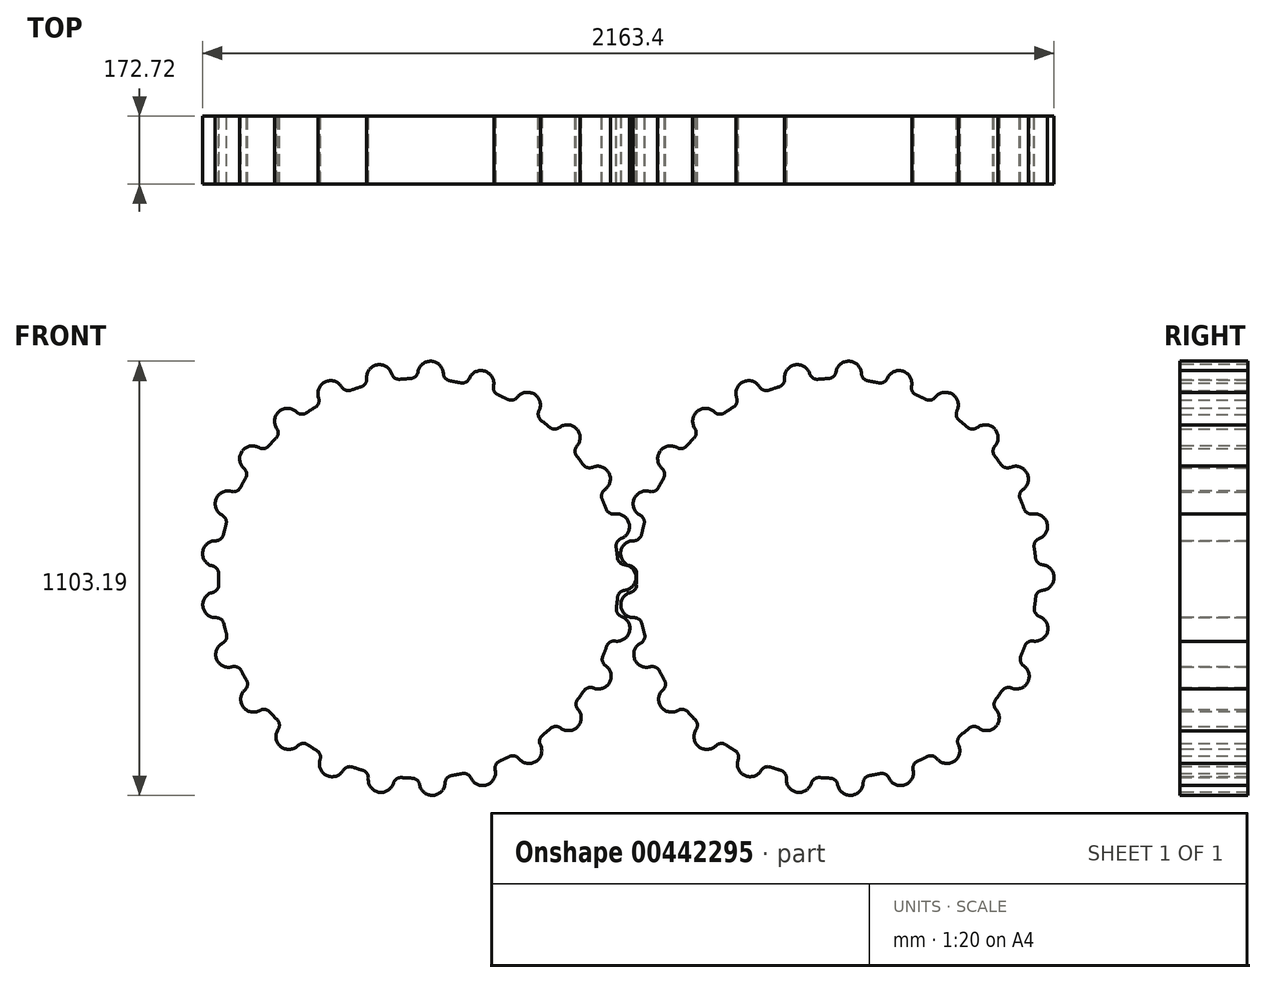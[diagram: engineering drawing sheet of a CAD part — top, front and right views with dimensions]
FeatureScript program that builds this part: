
annotation { "Feature Type Name" : "Feature", "Feature Type Description" : "" }
export const myFeature = defineFeature(function(context is Context, id is Id, definition is map)
    precondition{}
    {
        {
            var Q0;
            Q0=qCreatedBy(makeId("Front.planeOp"),FACE);
            var sketch = newSketch(context, id + "F0", { "sketchPlane" : qUnion([Q0])});
            skArc(sketch, "E0", {"start": v(0, 508) * mm, "mid": v(-33.99, 506.86) * mm, "end": v(-67.82, 503.45) * mm});
            skArc(sketch, "E1", {"start": v(59.51, 504.5) * mm, "mid": v(32.42, 551.67) * mm, "end": v(0, 508) * mm});
            skArc(sketch, "E2.1.0", {"start": v(-67.82, 503.45) * mm, "mid": v(-105.79, 542.4) * mm, "end": v(-126.33, 492.04) * mm});
            skArc(sketch, "E2.2.0", {"start": v(-190.9, 470.77) * mm, "mid": v(-237.35, 499.05) * mm, "end": v(-244.73, 445.16) * mm});
            skArc(sketch, "E2.3.0", {"start": v(-301.97, 408.5) * mm, "mid": v(-354, 424.35) * mm, "end": v(-347.75, 370.32) * mm});
            skArc(sketch, "E2.4.0", {"start": v(-394.08, 320.57) * mm, "mid": v(-448.42, 322.98) * mm, "end": v(-428.92, 272.2) * mm});
            skArc(sketch, "E2.5.0", {"start": v(-461.42, 212.5) * mm, "mid": v(-514.65, 201.31) * mm, "end": v(-483.14, 156.98) * mm});
            skArc(sketch, "E2.6.0", {"start": v(-499.77, 91.07) * mm, "mid": v(-548.54, 67) * mm, "end": v(-507, 31.9) * mm});
            skArc(sketch, "E2.7.0", {"start": v(-506.72, -36.08) * mm, "mid": v(-547.97, -71.52) * mm, "end": v(-499, -95.19) * mm});
            skArc(sketch, "E2.8.0", {"start": v(-481.83, -160.96) * mm, "mid": v(-512.97, -205.55) * mm, "end": v(-459.65, -216.3) * mm});
            skArc(sketch, "E2.9.0", {"start": v(-426.66, -275.73) * mm, "mid": v(-445.74, -326.66) * mm, "end": v(-391.42, -323.81) * mm});
            skArc(sketch, "E2.10.0", {"start": v(-344.68, -373.17) * mm, "mid": v(-350.5, -427.25) * mm, "end": v(-298.6, -410.98) * mm});
            skArc(sketch, "E2.11.0", {"start": v(-241.05, -447.17) * mm, "mid": v(-233.23, -501) * mm, "end": v(-187, -472.33) * mm});
            skArc(sketch, "E2.12.0", {"start": v(-122.27, -493.07) * mm, "mid": v(-101.31, -543.26) * mm, "end": v(-63.67, -504) * mm});
            skArc(sketch, "E2.13.0", {"start": v(4.19, -507.98) * mm, "mid": v(36.97, -551.38) * mm, "end": v(63.67, -504) * mm});
            skArc(sketch, "E2.14.0", {"start": v(130.39, -490.98) * mm, "mid": v(172.94, -524.87) * mm, "end": v(187, -472.33) * mm});
            skArc(sketch, "E2.15.0", {"start": v(248.4, -443.13) * mm, "mid": v(298.03, -465.37) * mm, "end": v(298.6, -410.98) * mm});
            skArc(sketch, "E2.16.0", {"start": v(350.8, -367.44) * mm, "mid": v(404.4, -376.63) * mm, "end": v(391.42, -323.81) * mm});
            skArc(sketch, "E2.17.0", {"start": v(431.15, -268.65) * mm, "mid": v(485.36, -264.23) * mm, "end": v(459.65, -216.3) * mm});
            skArc(sketch, "E2.18.0", {"start": v(484.42, -153) * mm, "mid": v(535.82, -135.22) * mm, "end": v(499, -95.19) * mm});
            skArc(sketch, "E2.19.0", {"start": v(507.24, -27.71) * mm, "mid": v(552.62, 2.28) * mm, "end": v(507, 31.9) * mm});
            skArc(sketch, "E2.20.0", {"start": v(498.2, 99.3) * mm, "mid": v(534.69, 139.64) * mm, "end": v(483.14, 156.98) * mm});
            skArc(sketch, "E2.21.0", {"start": v(457.85, 220.08) * mm, "mid": v(483.16, 268.22) * mm, "end": v(428.92, 272.2) * mm});
            skArc(sketch, "E2.22.0", {"start": v(388.74, 327.03) * mm, "mid": v(401.28, 379.95) * mm, "end": v(347.75, 370.32) * mm});
            skArc(sketch, "E2.23.0", {"start": v(295.2, 413.43) * mm, "mid": v(294.18, 467.81) * mm, "end": v(244.73, 445.16) * mm});
            skArc(sketch, "E2.24.0", {"start": v(183.1, 473.85) * mm, "mid": v(168.6, 526.27) * mm, "end": v(126.33, 492.04) * mm});
            skArc(sketch, "E3.trimOffspring", {"start": v(-126.33, 492.04) * mm, "mid": v(-158.97, 482.49) * mm, "end": v(-190.9, 470.77) * mm});
            skArc(sketch, "E4.trimOffspring", {"start": v(-244.73, 445.16) * mm, "mid": v(-273.97, 427.8) * mm, "end": v(-301.97, 408.5) * mm});
            skArc(sketch, "E5.trimOffspring", {"start": v(-347.75, 370.32) * mm, "mid": v(-371.75, 346.22) * mm, "end": v(-394.08, 320.57) * mm});
            skArc(sketch, "E6.trimOffspring", {"start": v(-428.92, 272.2) * mm, "mid": v(-446.17, 242.9) * mm, "end": v(-461.42, 212.5) * mm});
            skArc(sketch, "E7.trimOffspring", {"start": v(-483.14, 156.98) * mm, "mid": v(-492.56, 124.3) * mm, "end": v(-499.77, 91.07) * mm});
            skArc(sketch, "E8.trimOffspring", {"start": v(-507, 31.9) * mm, "mid": v(-508, -2.1) * mm, "end": v(-506.72, -36.08) * mm});
            skArc(sketch, "E9.trimOffspring", {"start": v(-499, -95.19) * mm, "mid": v(-491.52, -128.36) * mm, "end": v(-481.83, -160.96) * mm});
            skArc(sketch, "E10.trimOffspring", {"start": v(-459.65, -216.3) * mm, "mid": v(-444.15, -246.56) * mm, "end": v(-426.66, -275.73) * mm});
            skArc(sketch, "E11.trimOffspring", {"start": v(-391.42, -323.81) * mm, "mid": v(-368.88, -349.27) * mm, "end": v(-344.68, -373.17) * mm});
            skArc(sketch, "E12.trimOffspring", {"start": v(-298.6, -410.98) * mm, "mid": v(-270.43, -430.04) * mm, "end": v(-241.05, -447.17) * mm});
            skArc(sketch, "E13.trimOffspring", {"start": v(-187, -472.33) * mm, "mid": v(-154.99, -483.78) * mm, "end": v(-122.27, -493.07) * mm});
            skArc(sketch, "E14.trimOffspring", {"start": v(-63.67, -504) * mm, "mid": v(-29.8, -507.12) * mm, "end": v(4.19, -507.98) * mm});
            skArc(sketch, "E15.trimOffspring", {"start": v(63.67, -504) * mm, "mid": v(97.25, -498.6) * mm, "end": v(130.39, -490.98) * mm});
            skArc(sketch, "E16.trimOffspring", {"start": v(187, -472.33) * mm, "mid": v(218.19, -458.76) * mm, "end": v(248.4, -443.13) * mm});
            skArc(sketch, "E17.trimOffspring", {"start": v(298.6, -410.98) * mm, "mid": v(325.42, -390.08) * mm, "end": v(350.8, -367.44) * mm});
            skArc(sketch, "E18.trimOffspring", {"start": v(391.42, -323.81) * mm, "mid": v(412.2, -296.9) * mm, "end": v(431.15, -268.65) * mm});
            skArc(sketch, "E19.trimOffspring", {"start": v(459.65, -216.3) * mm, "mid": v(473.1, -185.06) * mm, "end": v(484.42, -153) * mm});
            skArc(sketch, "E20.trimOffspring", {"start": v(499, -95.19) * mm, "mid": v(504.25, -61.6) * mm, "end": v(507.24, -27.71) * mm});
            skArc(sketch, "E21.trimOffspring", {"start": v(507, 31.9) * mm, "mid": v(503.73, 65.75) * mm, "end": v(498.2, 99.3) * mm});
            skArc(sketch, "E22.trimOffspring", {"start": v(483.14, 156.98) * mm, "mid": v(471.55, 188.95) * mm, "end": v(457.85, 220.08) * mm});
            skArc(sketch, "E23.trimOffspring", {"start": v(428.92, 272.2) * mm, "mid": v(409.75, 300.29) * mm, "end": v(388.74, 327.03) * mm});
            skArc(sketch, "E24.trimOffspring", {"start": v(347.75, 370.32) * mm, "mid": v(322.2, 392.75) * mm, "end": v(295.2, 413.43) * mm});
            skArc(sketch, "E25.trimOffspring", {"start": v(244.73, 445.16) * mm, "mid": v(214.4, 460.54) * mm, "end": v(183.1, 473.85) * mm});
            skArc(sketch, "E26.trimOffspring", {"start": v(126.33, 492.04) * mm, "mid": v(93.13, 499.4) * mm, "end": v(59.51, 504.5) * mm});
            skSolve(sketch);
        }
        {
            var Q0;
            Q0=makeQuery(id+"F0.imprint","IMPRINT",FACE,{"disambiguationData":[TD([[makeQuery(id+"F0.imprint","IMPRINT",EDGE,{"derivedFrom":sQuery(id+"F0.wireOp",EDGE,"E0")}),1.0]])]});
            extrude(context, id + "F1", {"entities" : qUnion([Q0]), "oppositeDirection" : true, "depth" : 172.72 * mm});
        }
        {
            var Q0;
            Q0=makeQuery(id+"F1.opExtrude","SWEPT_EDGE",EDGE,{"disambiguationData":[OSD([sQuery(id+"F0.wireOp",EDGE,"E2.5.0"),sQuery(id+"F0.wireOp",EDGE,"E6.trimOffspring")])]});
            var Q1;
            Q1=makeQuery(id+"F1.opExtrude","SWEPT_EDGE",EDGE,{"disambiguationData":[OSD([sQuery(id+"F0.wireOp",EDGE,"E2.4.0"),sQuery(id+"F0.wireOp",EDGE,"E5.trimOffspring")])]});
            var Q2;
            Q2=makeQuery(id+"F1.opExtrude","SWEPT_EDGE",EDGE,{"disambiguationData":[OSD([sQuery(id+"F0.wireOp",EDGE,"E2.3.0"),sQuery(id+"F0.wireOp",EDGE,"E4.trimOffspring")])]});
            var Q3;
            Q3=makeQuery(id+"F1.opExtrude","SWEPT_EDGE",EDGE,{"disambiguationData":[OSD([sQuery(id+"F0.wireOp",EDGE,"E2.6.0"),sQuery(id+"F0.wireOp",EDGE,"E7.trimOffspring")])]});
            var Q4;
            Q4=makeQuery(id+"F1.opExtrude","SWEPT_EDGE",EDGE,{"disambiguationData":[OSD([sQuery(id+"F0.wireOp",EDGE,"E2.7.0"),sQuery(id+"F0.wireOp",EDGE,"E8.trimOffspring")])]});
            var Q5;
            Q5=makeQuery(id+"F1.opExtrude","SWEPT_EDGE",EDGE,{"disambiguationData":[OSD([sQuery(id+"F0.wireOp",EDGE,"E2.7.0"),sQuery(id+"F0.wireOp",EDGE,"E9.trimOffspring")])]});
            var Q6;
            Q6=makeQuery(id+"F1.opExtrude","SWEPT_EDGE",EDGE,{"disambiguationData":[OSD([sQuery(id+"F0.wireOp",EDGE,"E2.8.0"),sQuery(id+"F0.wireOp",EDGE,"E10.trimOffspring")])]});
            var Q7;
            Q7=makeQuery(id+"F1.opExtrude","SWEPT_EDGE",EDGE,{"disambiguationData":[OSD([sQuery(id+"F0.wireOp",EDGE,"E2.9.0"),sQuery(id+"F0.wireOp",EDGE,"E11.trimOffspring")])]});
            var Q8;
            Q8=makeQuery(id+"F1.opExtrude","SWEPT_EDGE",EDGE,{"disambiguationData":[OSD([sQuery(id+"F0.wireOp",EDGE,"E2.13.0"),sQuery(id+"F0.wireOp",EDGE,"E14.trimOffspring")])]});
            var Q9;
            Q9=makeQuery(id+"F1.opExtrude","SWEPT_EDGE",EDGE,{"disambiguationData":[OSD([sQuery(id+"F0.wireOp",EDGE,"E2.14.0"),sQuery(id+"F0.wireOp",EDGE,"E15.trimOffspring")])]});
            var Q10;
            Q10=makeQuery(id+"F1.opExtrude","SWEPT_EDGE",EDGE,{"disambiguationData":[OSD([sQuery(id+"F0.wireOp",EDGE,"E2.15.0"),sQuery(id+"F0.wireOp",EDGE,"E16.trimOffspring")])]});
            var Q11;
            Q11=makeQuery(id+"F1.opExtrude","SWEPT_EDGE",EDGE,{"disambiguationData":[OSD([sQuery(id+"F0.wireOp",EDGE,"E2.9.0"),sQuery(id+"F0.wireOp",EDGE,"E10.trimOffspring")])]});
            var Q12;
            Q12=makeQuery(id+"F1.opExtrude","SWEPT_EDGE",EDGE,{"disambiguationData":[OSD([sQuery(id+"F0.wireOp",EDGE,"E2.10.0"),sQuery(id+"F0.wireOp",EDGE,"E11.trimOffspring")])]});
            var Q13;
            Q13=makeQuery(id+"F1.opExtrude","SWEPT_EDGE",EDGE,{"disambiguationData":[OSD([sQuery(id+"F0.wireOp",EDGE,"E2.11.0"),sQuery(id+"F0.wireOp",EDGE,"E12.trimOffspring")])]});
            var Q14;
            Q14=makeQuery(id+"F1.opExtrude","SWEPT_EDGE",EDGE,{"disambiguationData":[OSD([sQuery(id+"F0.wireOp",EDGE,"E2.12.0"),sQuery(id+"F0.wireOp",EDGE,"E13.trimOffspring")])]});
            var Q15;
            Q15=makeQuery(id+"F1.opExtrude","SWEPT_EDGE",EDGE,{"disambiguationData":[OSD([sQuery(id+"F0.wireOp",EDGE,"E2.12.0"),sQuery(id+"F0.wireOp",EDGE,"E14.trimOffspring")])]});
            var Q16;
            Q16=makeQuery(id+"F1.opExtrude","SWEPT_EDGE",EDGE,{"disambiguationData":[OSD([sQuery(id+"F0.wireOp",EDGE,"E2.13.0"),sQuery(id+"F0.wireOp",EDGE,"E15.trimOffspring")])]});
            var Q17;
            Q17=makeQuery(id+"F1.opExtrude","SWEPT_EDGE",EDGE,{"disambiguationData":[OSD([sQuery(id+"F0.wireOp",EDGE,"E2.14.0"),sQuery(id+"F0.wireOp",EDGE,"E16.trimOffspring")])]});
            var Q18;
            Q18=makeQuery(id+"F1.opExtrude","SWEPT_EDGE",EDGE,{"disambiguationData":[OSD([sQuery(id+"F0.wireOp",EDGE,"E2.15.0"),sQuery(id+"F0.wireOp",EDGE,"E17.trimOffspring")])]});
            var Q19;
            Q19=makeQuery(id+"F1.opExtrude","SWEPT_EDGE",EDGE,{"disambiguationData":[OSD([sQuery(id+"F0.wireOp",EDGE,"E2.16.0"),sQuery(id+"F0.wireOp",EDGE,"E18.trimOffspring")])]});
            var Q20;
            Q20=makeQuery(id+"F1.opExtrude","SWEPT_EDGE",EDGE,{"disambiguationData":[OSD([sQuery(id+"F0.wireOp",EDGE,"E2.17.0"),sQuery(id+"F0.wireOp",EDGE,"E19.trimOffspring")])]});
            var Q21;
            Q21=makeQuery(id+"F1.opExtrude","SWEPT_EDGE",EDGE,{"disambiguationData":[OSD([sQuery(id+"F0.wireOp",EDGE,"E2.18.0"),sQuery(id+"F0.wireOp",EDGE,"E20.trimOffspring")])]});
            var Q22;
            Q22=makeQuery(id+"F1.opExtrude","SWEPT_EDGE",EDGE,{"disambiguationData":[OSD([sQuery(id+"F0.wireOp",EDGE,"E2.19.0"),sQuery(id+"F0.wireOp",EDGE,"E21.trimOffspring")])]});
            var Q23;
            Q23=makeQuery(id+"F1.opExtrude","SWEPT_EDGE",EDGE,{"disambiguationData":[OSD([sQuery(id+"F0.wireOp",EDGE,"E2.20.0"),sQuery(id+"F0.wireOp",EDGE,"E22.trimOffspring")])]});
            var Q24;
            Q24=makeQuery(id+"F1.opExtrude","SWEPT_EDGE",EDGE,{"disambiguationData":[OSD([sQuery(id+"F0.wireOp",EDGE,"E2.21.0"),sQuery(id+"F0.wireOp",EDGE,"E23.trimOffspring")])]});
            var Q25;
            Q25=makeQuery(id+"F1.opExtrude","SWEPT_EDGE",EDGE,{"disambiguationData":[OSD([sQuery(id+"F0.wireOp",EDGE,"E2.22.0"),sQuery(id+"F0.wireOp",EDGE,"E24.trimOffspring")])]});
            var Q26;
            Q26=makeQuery(id+"F1.opExtrude","SWEPT_EDGE",EDGE,{"disambiguationData":[OSD([sQuery(id+"F0.wireOp",EDGE,"E2.23.0"),sQuery(id+"F0.wireOp",EDGE,"E25.trimOffspring")])]});
            var Q27;
            Q27=makeQuery(id+"F1.opExtrude","SWEPT_EDGE",EDGE,{"disambiguationData":[OSD([sQuery(id+"F0.wireOp",EDGE,"E2.24.0"),sQuery(id+"F0.wireOp",EDGE,"E26.trimOffspring")])]});
            var Q28;
            Q28=makeQuery(id+"F1.opExtrude","SWEPT_EDGE",EDGE,{"disambiguationData":[OSD([sQuery(id+"F0.wireOp",EDGE,"E0"),sQuery(id+"F0.wireOp",EDGE,"E1")])]});
            var Q29;
            Q29=makeQuery(id+"F1.opExtrude","SWEPT_EDGE",EDGE,{"disambiguationData":[OSD([sQuery(id+"F0.wireOp",EDGE,"E2.1.0"),sQuery(id+"F0.wireOp",EDGE,"E3.trimOffspring")])]});
            var Q30;
            Q30=makeQuery(id+"F1.opExtrude","SWEPT_EDGE",EDGE,{"disambiguationData":[OSD([sQuery(id+"F0.wireOp",EDGE,"E2.2.0"),sQuery(id+"F0.wireOp",EDGE,"E4.trimOffspring")])]});
            var Q31;
            Q31=makeQuery(id+"F1.opExtrude","SWEPT_EDGE",EDGE,{"disambiguationData":[OSD([sQuery(id+"F0.wireOp",EDGE,"E2.2.0"),sQuery(id+"F0.wireOp",EDGE,"E3.trimOffspring")])]});
            var Q32;
            Q32=makeQuery(id+"F1.opExtrude","SWEPT_EDGE",EDGE,{"disambiguationData":[OSD([sQuery(id+"F0.wireOp",EDGE,"E0"),sQuery(id+"F0.wireOp",EDGE,"E2.1.0")])]});
            var Q33;
            Q33=makeQuery(id+"F1.opExtrude","SWEPT_EDGE",EDGE,{"disambiguationData":[OSD([sQuery(id+"F0.wireOp",EDGE,"E1"),sQuery(id+"F0.wireOp",EDGE,"E26.trimOffspring")])]});
            var Q34;
            Q34=makeQuery(id+"F1.opExtrude","SWEPT_EDGE",EDGE,{"disambiguationData":[OSD([sQuery(id+"F0.wireOp",EDGE,"E2.24.0"),sQuery(id+"F0.wireOp",EDGE,"E25.trimOffspring")])]});
            var Q35;
            Q35=makeQuery(id+"F1.opExtrude","SWEPT_EDGE",EDGE,{"disambiguationData":[OSD([sQuery(id+"F0.wireOp",EDGE,"E2.23.0"),sQuery(id+"F0.wireOp",EDGE,"E24.trimOffspring")])]});
            var Q36;
            Q36=makeQuery(id+"F1.opExtrude","SWEPT_EDGE",EDGE,{"disambiguationData":[OSD([sQuery(id+"F0.wireOp",EDGE,"E2.22.0"),sQuery(id+"F0.wireOp",EDGE,"E23.trimOffspring")])]});
            var Q37;
            Q37=makeQuery(id+"F1.opExtrude","SWEPT_EDGE",EDGE,{"disambiguationData":[OSD([sQuery(id+"F0.wireOp",EDGE,"E2.21.0"),sQuery(id+"F0.wireOp",EDGE,"E22.trimOffspring")])]});
            var Q38;
            Q38=makeQuery(id+"F1.opExtrude","SWEPT_EDGE",EDGE,{"disambiguationData":[OSD([sQuery(id+"F0.wireOp",EDGE,"E2.20.0"),sQuery(id+"F0.wireOp",EDGE,"E21.trimOffspring")])]});
            var Q39;
            Q39=makeQuery(id+"F1.opExtrude","SWEPT_EDGE",EDGE,{"disambiguationData":[OSD([sQuery(id+"F0.wireOp",EDGE,"E2.19.0"),sQuery(id+"F0.wireOp",EDGE,"E20.trimOffspring")])]});
            var Q40;
            Q40=makeQuery(id+"F1.opExtrude","SWEPT_EDGE",EDGE,{"disambiguationData":[OSD([sQuery(id+"F0.wireOp",EDGE,"E2.18.0"),sQuery(id+"F0.wireOp",EDGE,"E19.trimOffspring")])]});
            var Q41;
            Q41=makeQuery(id+"F1.opExtrude","SWEPT_EDGE",EDGE,{"disambiguationData":[OSD([sQuery(id+"F0.wireOp",EDGE,"E2.17.0"),sQuery(id+"F0.wireOp",EDGE,"E18.trimOffspring")])]});
            var Q42;
            Q42=makeQuery(id+"F1.opExtrude","SWEPT_EDGE",EDGE,{"disambiguationData":[OSD([sQuery(id+"F0.wireOp",EDGE,"E2.16.0"),sQuery(id+"F0.wireOp",EDGE,"E17.trimOffspring")])]});
            var Q43;
            Q43=makeQuery(id+"F1.opExtrude","SWEPT_EDGE",EDGE,{"disambiguationData":[OSD([sQuery(id+"F0.wireOp",EDGE,"E2.6.0"),sQuery(id+"F0.wireOp",EDGE,"E8.trimOffspring")])]});
            var Q44;
            Q44=makeQuery(id+"F1.opExtrude","SWEPT_EDGE",EDGE,{"disambiguationData":[OSD([sQuery(id+"F0.wireOp",EDGE,"E2.5.0"),sQuery(id+"F0.wireOp",EDGE,"E7.trimOffspring")])]});
            var Q45;
            Q45=makeQuery(id+"F1.opExtrude","SWEPT_EDGE",EDGE,{"disambiguationData":[OSD([sQuery(id+"F0.wireOp",EDGE,"E2.4.0"),sQuery(id+"F0.wireOp",EDGE,"E6.trimOffspring")])]});
            var Q46;
            Q46=makeQuery(id+"F1.opExtrude","SWEPT_EDGE",EDGE,{"disambiguationData":[OSD([sQuery(id+"F0.wireOp",EDGE,"E2.8.0"),sQuery(id+"F0.wireOp",EDGE,"E9.trimOffspring")])]});
            var Q47;
            Q47=makeQuery(id+"F1.opExtrude","SWEPT_EDGE",EDGE,{"disambiguationData":[OSD([sQuery(id+"F0.wireOp",EDGE,"E2.3.0"),sQuery(id+"F0.wireOp",EDGE,"E5.trimOffspring")])]});
            var Q48;
            Q48=makeQuery(id+"F1.opExtrude","SWEPT_EDGE",EDGE,{"disambiguationData":[OSD([sQuery(id+"F0.wireOp",EDGE,"E2.10.0"),sQuery(id+"F0.wireOp",EDGE,"E12.trimOffspring")])]});
            var Q49;
            Q49=makeQuery(id+"F1.opExtrude","SWEPT_EDGE",EDGE,{"disambiguationData":[OSD([sQuery(id+"F0.wireOp",EDGE,"E2.11.0"),sQuery(id+"F0.wireOp",EDGE,"E13.trimOffspring")])]});
            fillet(context, id + "F2", {"entities" : qUnion([Q0, Q1, Q2, Q3, Q4, Q5, Q6, Q7, Q8, Q9, Q10, Q11, Q12, Q13, Q14, Q15, Q16, Q17, Q18, Q19, Q20, Q21, Q22, Q23, Q24, Q25, Q26, Q27, Q28, Q29, Q30, Q31, Q32, Q33, Q34, Q35, Q36, Q37, Q38, Q39, Q40, Q41, Q42, Q43, Q44, Q45, Q46, Q47, Q48, Q49]), "radius" : 20 * mm, "tangentPropagation" : true, "allowEdgeOverflow" : false});
        }
        {
            var Q0;
            Q0=makeQuery(id+"F1.opExtrude","SWEPT_BODY",BODY,{"disambiguationData":[OSD([sQuery(id+"F0.wireOp",EDGE,"E0"),sQuery(id+"F0.wireOp",EDGE,"E1"),sQuery(id+"F0.wireOp",EDGE,"E2.1.0"),sQuery(id+"F0.wireOp",EDGE,"E2.2.0"),sQuery(id+"F0.wireOp",EDGE,"E2.3.0"),sQuery(id+"F0.wireOp",EDGE,"E2.4.0"),sQuery(id+"F0.wireOp",EDGE,"E2.5.0"),sQuery(id+"F0.wireOp",EDGE,"E2.6.0"),sQuery(id+"F0.wireOp",EDGE,"E2.7.0"),sQuery(id+"F0.wireOp",EDGE,"E2.8.0"),sQuery(id+"F0.wireOp",EDGE,"E2.9.0"),sQuery(id+"F0.wireOp",EDGE,"E2.10.0"),sQuery(id+"F0.wireOp",EDGE,"E2.11.0"),sQuery(id+"F0.wireOp",EDGE,"E2.12.0"),sQuery(id+"F0.wireOp",EDGE,"E2.13.0"),sQuery(id+"F0.wireOp",EDGE,"E2.14.0"),sQuery(id+"F0.wireOp",EDGE,"E2.15.0"),sQuery(id+"F0.wireOp",EDGE,"E2.16.0"),sQuery(id+"F0.wireOp",EDGE,"E2.17.0"),sQuery(id+"F0.wireOp",EDGE,"E2.18.0"),sQuery(id+"F0.wireOp",EDGE,"E2.19.0"),sQuery(id+"F0.wireOp",EDGE,"E2.20.0"),sQuery(id+"F0.wireOp",EDGE,"E2.21.0"),sQuery(id+"F0.wireOp",EDGE,"E2.22.0"),sQuery(id+"F0.wireOp",EDGE,"E2.23.0"),sQuery(id+"F0.wireOp",EDGE,"E2.24.0"),sQuery(id+"F0.wireOp",EDGE,"E3.trimOffspring"),sQuery(id+"F0.wireOp",EDGE,"E4.trimOffspring"),sQuery(id+"F0.wireOp",EDGE,"E5.trimOffspring"),sQuery(id+"F0.wireOp",EDGE,"E6.trimOffspring"),sQuery(id+"F0.wireOp",EDGE,"E7.trimOffspring"),sQuery(id+"F0.wireOp",EDGE,"E8.trimOffspring"),sQuery(id+"F0.wireOp",EDGE,"E9.trimOffspring"),sQuery(id+"F0.wireOp",EDGE,"E10.trimOffspring"),sQuery(id+"F0.wireOp",EDGE,"E11.trimOffspring"),sQuery(id+"F0.wireOp",EDGE,"E12.trimOffspring"),sQuery(id+"F0.wireOp",EDGE,"E13.trimOffspring"),sQuery(id+"F0.wireOp",EDGE,"E14.trimOffspring"),sQuery(id+"F0.wireOp",EDGE,"E15.trimOffspring"),sQuery(id+"F0.wireOp",EDGE,"E16.trimOffspring"),sQuery(id+"F0.wireOp",EDGE,"E17.trimOffspring"),sQuery(id+"F0.wireOp",EDGE,"E18.trimOffspring"),sQuery(id+"F0.wireOp",EDGE,"E19.trimOffspring"),sQuery(id+"F0.wireOp",EDGE,"E20.trimOffspring"),sQuery(id+"F0.wireOp",EDGE,"E21.trimOffspring"),sQuery(id+"F0.wireOp",EDGE,"E22.trimOffspring"),sQuery(id+"F0.wireOp",EDGE,"E23.trimOffspring"),sQuery(id+"F0.wireOp",EDGE,"E24.trimOffspring"),sQuery(id+"F0.wireOp",EDGE,"E25.trimOffspring"),sQuery(id+"F0.wireOp",EDGE,"E26.trimOffspring")])]});
            transform(context, id + "F3", {"entities" : qUnion([Q0]), "transformType" : TransformType.TRANSLATION_3D, "dx" : 1020 * mm, "dy" : 0 * mm, "dz" : 0 * mm, "makeCopy" : true});
        }
        {
            var Q0;
            Q0=makeQuery(id+"F3.opPattern","COPY",BODY,{"derivedFrom":makeQuery(id+"F1.opExtrude","SWEPT_BODY",BODY,{"disambiguationData":[OSD([sQuery(id+"F0.wireOp",EDGE,"E0"),sQuery(id+"F0.wireOp",EDGE,"E1"),sQuery(id+"F0.wireOp",EDGE,"E2.1.0"),sQuery(id+"F0.wireOp",EDGE,"E2.2.0"),sQuery(id+"F0.wireOp",EDGE,"E2.3.0"),sQuery(id+"F0.wireOp",EDGE,"E2.4.0"),sQuery(id+"F0.wireOp",EDGE,"E2.5.0"),sQuery(id+"F0.wireOp",EDGE,"E2.6.0"),sQuery(id+"F0.wireOp",EDGE,"E2.7.0"),sQuery(id+"F0.wireOp",EDGE,"E2.8.0"),sQuery(id+"F0.wireOp",EDGE,"E2.9.0"),sQuery(id+"F0.wireOp",EDGE,"E2.10.0"),sQuery(id+"F0.wireOp",EDGE,"E2.11.0"),sQuery(id+"F0.wireOp",EDGE,"E2.12.0"),sQuery(id+"F0.wireOp",EDGE,"E2.13.0"),sQuery(id+"F0.wireOp",EDGE,"E2.14.0"),sQuery(id+"F0.wireOp",EDGE,"E2.15.0"),sQuery(id+"F0.wireOp",EDGE,"E2.16.0"),sQuery(id+"F0.wireOp",EDGE,"E2.17.0"),sQuery(id+"F0.wireOp",EDGE,"E2.18.0"),sQuery(id+"F0.wireOp",EDGE,"E2.19.0"),sQuery(id+"F0.wireOp",EDGE,"E2.20.0"),sQuery(id+"F0.wireOp",EDGE,"E2.21.0"),sQuery(id+"F0.wireOp",EDGE,"E2.22.0"),sQuery(id+"F0.wireOp",EDGE,"E2.23.0"),sQuery(id+"F0.wireOp",EDGE,"E2.24.0"),sQuery(id+"F0.wireOp",EDGE,"E3.trimOffspring"),sQuery(id+"F0.wireOp",EDGE,"E4.trimOffspring"),sQuery(id+"F0.wireOp",EDGE,"E5.trimOffspring"),sQuery(id+"F0.wireOp",EDGE,"E6.trimOffspring"),sQuery(id+"F0.wireOp",EDGE,"E7.trimOffspring"),sQuery(id+"F0.wireOp",EDGE,"E8.trimOffspring"),sQuery(id+"F0.wireOp",EDGE,"E9.trimOffspring"),sQuery(id+"F0.wireOp",EDGE,"E10.trimOffspring"),sQuery(id+"F0.wireOp",EDGE,"E11.trimOffspring"),sQuery(id+"F0.wireOp",EDGE,"E12.trimOffspring"),sQuery(id+"F0.wireOp",EDGE,"E13.trimOffspring"),sQuery(id+"F0.wireOp",EDGE,"E14.trimOffspring"),sQuery(id+"F0.wireOp",EDGE,"E15.trimOffspring"),sQuery(id+"F0.wireOp",EDGE,"E16.trimOffspring"),sQuery(id+"F0.wireOp",EDGE,"E17.trimOffspring"),sQuery(id+"F0.wireOp",EDGE,"E18.trimOffspring"),sQuery(id+"F0.wireOp",EDGE,"E19.trimOffspring"),sQuery(id+"F0.wireOp",EDGE,"E20.trimOffspring"),sQuery(id+"F0.wireOp",EDGE,"E21.trimOffspring"),sQuery(id+"F0.wireOp",EDGE,"E22.trimOffspring"),sQuery(id+"F0.wireOp",EDGE,"E23.trimOffspring"),sQuery(id+"F0.wireOp",EDGE,"E24.trimOffspring"),sQuery(id+"F0.wireOp",EDGE,"E25.trimOffspring"),sQuery(id+"F0.wireOp",EDGE,"E26.trimOffspring")])]}),"instanceName":"1"});
            transform(context, id + "F4", {"entities" : qUnion([Q0]), "transformType" : TransformType.TRANSLATION_3D, "dx" : 42 * mm, "dy" : 0 * mm, "dz" : 0 * mm, "makeCopy" : false});
        }
    });
